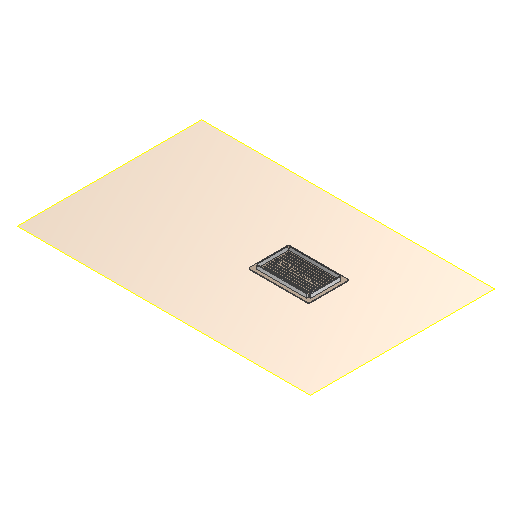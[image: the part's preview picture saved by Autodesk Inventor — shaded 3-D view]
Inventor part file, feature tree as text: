
AUTODESK INVENTOR PART (.ipt)
format: ipt  version: 2024.1 (Build 281209000, 209)  size: 571,392 bytes
history: native  units: mm
features: projected_geometry x13, extrude x4, sketch x4, other x2, plane x1, fillet x1, pattern_linear x1, reference x1
ambient origin geometry x8: Origin, YZ Plane, XZ Plane, XY Plane, X Axis, Y Axis, Z Axis, Center Point
bodies: Volumenkörper1 (feature_tree)
feature tree (27):
  plane  "Arbeitsebene1"
  extrude  "Extrusion1"  Depth=2.0mm
  extrude  "Extrusion2"  Depth=5.0mm
  extrude  "Extrusion3"  Depth=2.0mm
  extrude  "Extrusion4"  Depth=4.0mm
  fillet  "Rundung1"  Radius=1.0mm
  pattern_linear  "Rechteckige Anordnung1"  Spacing1=1.0mm  [1 undecoded]
  sketch  "Skizze1"  dims[d0=0.2mm d1=2.0mm]
  reference  "Referenz1"
  sketch  "Skizze2"  dims[d2=5.0mm d3=-0.872665mm d4=90.0mm]
  projected_geometry  "Projizierte Kontur1"
  projected_geometry  "Projizierte Kontur2"
  projected_geometry  "Projizierte Kontur3"
  projected_geometry  "Projizierte Kontur4"
  sketch  "Skizze3"  dims[d5=60.0mm d6=2.0mm]
  projected_geometry  "Projizierte Kontur5"
  sketch  "Skizze4"  dims[d7=72.0mm d8=42.0mm d9=1.0mm d10=0.0mm d11=1.0mm d12=0.0mm d13=2.0mm d14=2.0mm d15=1.0mm d16=0.0mm d17=0.9mm d18=100.0mm d20=4.0mm]
  projected_geometry  "Projizierte Kontur6"
  projected_geometry  "Projizierte Kontur7"
  projected_geometry  "Projizierte Kontur8"
  projected_geometry  "Projizierte Kontur9"
  projected_geometry  "Projizierte Kontur10"
  projected_geometry  "Projizierte Kontur11"
  projected_geometry  "Projizierte Kontur12"
  projected_geometry  "Projizierte Kontur13"
  other  "Assembly_Planktoscope_Uc2version_wormdrive_V3.iam"
  other  "BoxCotout:1"
note: 1 required parameter value undecoded (feature->parameter linkage not recoverable at this tier; creation-order binding heuristic only, values carry confidence <= 0.55)
